# Revit family: FU_Inspec_Add_Stool_4-3
name_source: partatom
category: Furniture
units: mm (PartAtom-declared; Revit-internal decimal feet)

## family parameters
Always vertical = Yes
Cut with Voids When Loaded = No
OmniClass Number = 23.40.20.00
OmniClass Title = General Furniture and Specialties
Room Calculation Point = No
Shared = No
Work Plane-Based = No

## types (2) — shared parameters
Assembly Code = E2020
Frame Material = Metal - Chrome - Polished
Keynote = 46.B
Manufacturer = Inspec
URL = https://inspecfurniture.com
zero-valued in all types: Default Elevation

## per-type parameters (varying)
| type | Description | Seat Material |
| add stool 4.4 | Counter stool with seat of upholstered molded wood and polyurethane foam, on a powder coated or chromium plated steel tubular frame. With chrome footrest | Fabric - Red |
| add stool 4.3 | Counter stool with seat of molded wood and polyurethane foam, on a powder coated or chromium plated steel cantilever frame. With chrome footrest | Plastic - Black |

note: column(s) folded — value = type name in every type: Model

## geometry (parser evidence)
native form markers: Blend x5, Sweep x2
no freeform markers — native parametric forms only
